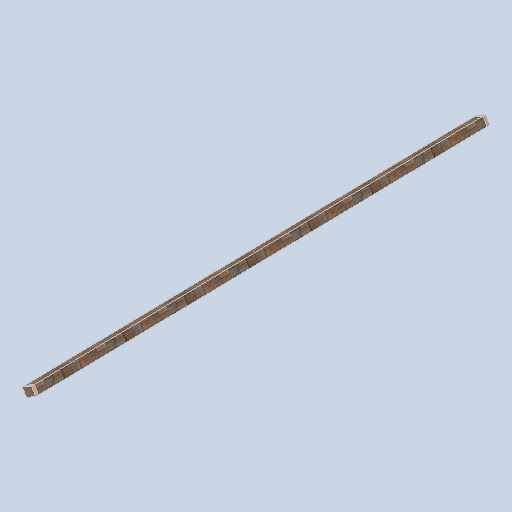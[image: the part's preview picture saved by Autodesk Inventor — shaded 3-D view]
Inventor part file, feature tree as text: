
AUTODESK INVENTOR PART (.ipt)
format: ipt  version: 2024.2 (Build 282272000, 272)  size: 134,144 bytes
history: native  units: in
note: dims shown in document units (in); Inventor stores cm internally (conversion verified against a paired STEP export)
features: sketch x4, other x3, plane x2
ambient origin geometry x8: Origin, YZ Plane, XZ Plane, XY Plane, X Axis, Y Axis, Z Axis, Center Point
bodies: Solid1 (feature_tree)
feature tree (9):
  other  "support_beam_segment_0105.ipt"
  other  "Solid1::support_beam_segment_0105.ipt"
  other  "TaggingFeature1"
  sketch  "Sketch1"  dims[d0=0.3937in]
  sketch  "Sketch2"
  sketch  "Sketch3"
  sketch  "Sketch4"
  plane  "Work Plane1"
  plane  "Work Plane2"
